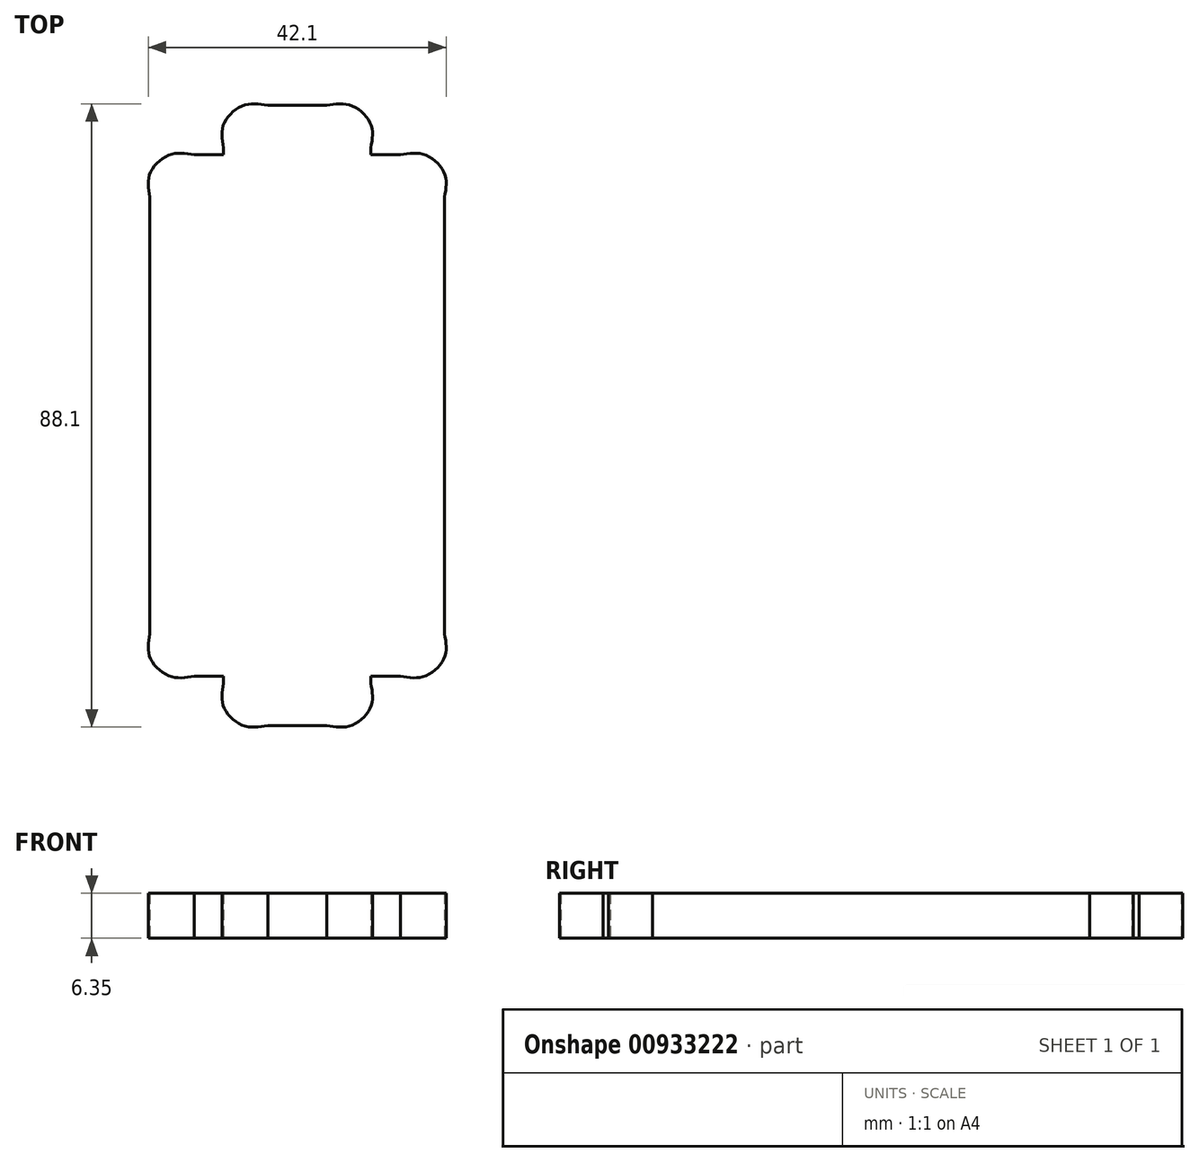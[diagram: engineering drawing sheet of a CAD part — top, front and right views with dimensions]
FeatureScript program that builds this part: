
annotation { "Feature Type Name" : "Feature", "Feature Type Description" : "" }
export const myFeature = defineFeature(function(context is Context, id is Id, definition is map)
    precondition{}
    {
        {
            var Q0;
            Q0=qCreatedBy(makeId("Top.planeOp"),FACE);
            var sketch = newSketch(context, id + "F0", { "sketchPlane" : qUnion([Q0])});
            skLineSegment(sketch, "E0", {"start": v(-10.41, 37.85) * mm, "end": v(-10.41, 36.85) * mm});
            skLineSegment(sketch, "E1", {"start": v(-10.41, 36.85) * mm, "end": v(-14.57, 36.85) * mm});
            skLineSegment(sketch, "E2", {"start": v(-20.82, 30.87) * mm, "end": v(-20.82, -30.88) * mm});
            skLineSegment(sketch, "E3", {"start": v(-14.57, -36.85) * mm, "end": v(-10.41, -36.85) * mm});
            skLineSegment(sketch, "E4", {"start": v(-10.41, -36.85) * mm, "end": v(-10.41, -37.85) * mm});
            skLineSegment(sketch, "E5", {"start": v(-4.17, -43.82) * mm, "end": v(4.16, -43.82) * mm});
            skLineSegment(sketch, "E6", {"start": v(10.4, -37.85) * mm, "end": v(10.4, -36.85) * mm});
            skLineSegment(sketch, "E7", {"start": v(10.4, -36.85) * mm, "end": v(14.57, -36.85) * mm});
            skLineSegment(sketch, "E8", {"start": v(20.82, -30.88) * mm, "end": v(20.82, 30.87) * mm});
            skLineSegment(sketch, "E9", {"start": v(14.57, 36.85) * mm, "end": v(10.4, 36.85) * mm});
            skLineSegment(sketch, "E10", {"start": v(10.4, 36.85) * mm, "end": v(10.4, 37.85) * mm});
            skLineSegment(sketch, "E11", {"start": v(4.16, 43.82) * mm, "end": v(-4.17, 43.82) * mm});
            skFitSpline(sketch, "E12", {"points": [v(-14.57, 36.85) * mm, v(-18.02, 36.85) * mm, v(-20.82, 34.17) * mm, v(-20.82, 30.87) * mm]});
            skFitSpline(sketch, "E13", {"points": [v(-20.82, -30.88) * mm, v(-20.82, -34.18) * mm, v(-18.02, -36.85) * mm, v(-14.57, -36.85) * mm]});
            skFitSpline(sketch, "E14", {"points": [v(-10.41, -37.85) * mm, v(-10.41, -41.15) * mm, v(-7.62, -43.82) * mm, v(-4.17, -43.82) * mm]});
            skFitSpline(sketch, "E15", {"points": [v(4.16, -43.82) * mm, v(7.6, -43.82) * mm, v(10.4, -41.15) * mm, v(10.4, -37.85) * mm]});
            skFitSpline(sketch, "E16", {"points": [v(14.57, -36.85) * mm, v(18.02, -36.85) * mm, v(20.82, -34.18) * mm, v(20.82, -30.88) * mm]});
            skFitSpline(sketch, "E17", {"points": [v(20.82, 30.87) * mm, v(20.82, 34.17) * mm, v(18.02, 36.85) * mm, v(14.57, 36.85) * mm]});
            skFitSpline(sketch, "E18", {"points": [v(10.4, 37.85) * mm, v(10.4, 41.15) * mm, v(7.6, 43.82) * mm, v(4.16, 43.82) * mm]});
            skFitSpline(sketch, "E19", {"points": [v(-4.17, 43.82) * mm, v(-7.62, 43.82) * mm, v(-10.41, 41.15) * mm, v(-10.41, 37.85) * mm]});
            skSolve(sketch);
        }
        {
            var Q0;
            Q0=makeQuery(id+"F0.imprint","IMPRINT",FACE,{"disambiguationData":[TD([[makeQuery(id+"F0.imprint","IMPRINT",EDGE,{"derivedFrom":sQuery(id+"F0.wireOp",EDGE,"E0")}),1.0]])]});
            extrude(context, id + "F1", {"entities" : qUnion([Q0]), "depth" : 6.35 * mm, "offsetDistance" : 25.4 * mm});
        }
    });
